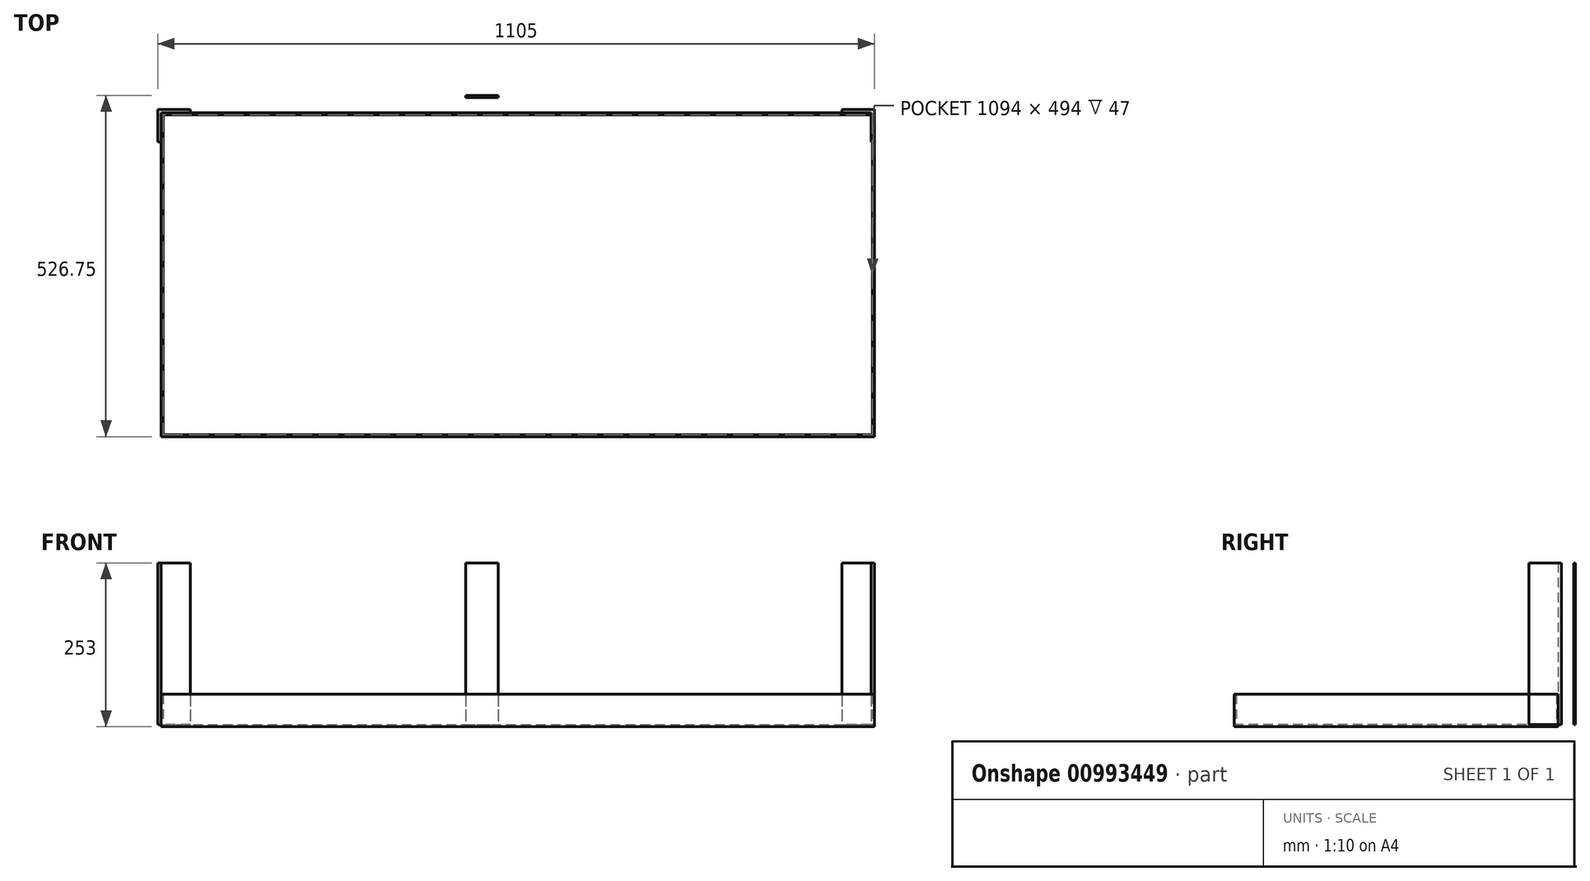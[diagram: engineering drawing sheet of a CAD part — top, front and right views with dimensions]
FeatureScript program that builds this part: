
annotation { "Feature Type Name" : "Feature", "Feature Type Description" : "" }
export const myFeature = defineFeature(function(context is Context, id is Id, definition is map)
    precondition{}
    {
        {
            var Q0;
            Q0=qCreatedBy(makeId("Top.planeOp"),FACE);
            var sketch = newSketch(context, id + "F0", { "sketchPlane" : qUnion([Q0])});
            skLineSegment(sketch, "E0.bottom", {"start": v(-561.99, 291.3) * mm, "end": v(538.01, 291.3) * mm});
            skLineSegment(sketch, "E0.top", {"start": v(-561.99, -208.7) * mm, "end": v(538.01, -208.7) * mm});
            skLineSegment(sketch, "E0.left", {"start": v(-561.99, 291.3) * mm, "end": v(-561.99, -208.7) * mm});
            skLineSegment(sketch, "E0.right", {"start": v(538.01, 291.3) * mm, "end": v(538.01, -208.7) * mm});
            skSolve(sketch);
        }
        {
            var Q0;
            Q0=makeQuery(id+"F0.imprint","IMPRINT",FACE,{"disambiguationData":[TD([[makeQuery(id+"F0.imprint","IMPRINT",EDGE,{"derivedFrom":sQuery(id+"F0.wireOp",EDGE,"E0.bottom")}),-1.0]])]});
            extrude(context, id + "F1", {"entities" : qUnion([Q0]), "depth" : 50 * mm, "offsetDistance" : 25 * mm});
        }
        {
            var Q0;
            Q0=makeQuery(id+"F1.opExtrude","CAP_FACE",FACE,{"disambiguationData":[OSD([sQuery(id+"F0.wireOp",EDGE,"E0.bottom"),sQuery(id+"F0.wireOp",EDGE,"E0.top"),sQuery(id+"F0.wireOp",EDGE,"E0.left"),sQuery(id+"F0.wireOp",EDGE,"E0.right")])],"isStart":false});
            shell(context, id + "F2", {"entities" : qUnion([Q0]), "thickness" : 3 * mm});
        }
        {
            var Q0;
            Q0=makeQuery(id+"F2.opShell","OFFSET_FACE",FACE,{"disambiguationData":[OSD([sQuery(id+"F0.wireOp",EDGE,"E0.bottom"),sQuery(id+"F0.wireOp",EDGE,"E0.top"),sQuery(id+"F0.wireOp",EDGE,"E0.left"),sQuery(id+"F0.wireOp",EDGE,"E0.right")])]});
            var sketch = newSketch(context, id + "F3", { "sketchPlane" : qUnion([Q0])});
            skLineSegment(sketch, "E1", {"start": v(-516.99, 291.3) * mm, "end": v(-516.99, 296.3) * mm});
            skLineSegment(sketch, "E2", {"start": v(-516.99, 296.3) * mm, "end": v(-566.99, 296.3) * mm});
            skLineSegment(sketch, "E3", {"start": v(-566.99, 296.3) * mm, "end": v(-566.99, 246.3) * mm});
            skLineSegment(sketch, "E4", {"start": v(-566.99, 246.3) * mm, "end": v(-561.99, 246.3) * mm});
            skLineSegment(sketch, "E5", {"start": v(-561.99, 246.3) * mm, "end": v(-561.99, 291.3) * mm});
            skLineSegment(sketch, "E6", {"start": v(-561.99, 291.3) * mm, "end": v(-516.99, 291.3) * mm});
            skSolve(sketch);
        }
        {
            var Q0;
            Q0=makeQuery(id+"F3.imprint","IMPRINT",FACE,{"disambiguationData":[TD([[makeQuery(id+"F3.imprint","IMPRINT",EDGE,{"derivedFrom":sQuery(id+"F3.wireOp",EDGE,"E1")}),1.0]])]});
            extrude(context, id + "F4", {"entities" : qUnion([Q0]), "depth" : 250 * mm, "offsetDistance" : 25 * mm});
        }
        {
            var Q0;
            Q0=makeQuery(id+"F4.opExtrude","SWEPT_BODY",BODY,{"disambiguationData":[OSD([sQuery(id+"F3.wireOp",EDGE,"E1"),sQuery(id+"F3.wireOp",EDGE,"E2"),sQuery(id+"F3.wireOp",EDGE,"E3"),sQuery(id+"F3.wireOp",EDGE,"E4"),sQuery(id+"F3.wireOp",EDGE,"E5"),sQuery(id+"F3.wireOp",EDGE,"E6")])]});
            transform(context, id + "F5", {"entities" : qUnion([Q0]), "transformType" : TransformType.TRANSLATION_3D, "dx" : 1105 * mm, "dy" : 0 * mm, "dz" : 0 * mm, "makeCopy" : true});
        }
        {
            var Q0;
            Q0=makeQuery(id+"F5.opPattern","COPY",BODY,{"derivedFrom":makeQuery(id+"F4.opExtrude","SWEPT_BODY",BODY,{"disambiguationData":[OSD([sQuery(id+"F3.wireOp",EDGE,"E1"),sQuery(id+"F3.wireOp",EDGE,"E2"),sQuery(id+"F3.wireOp",EDGE,"E3"),sQuery(id+"F3.wireOp",EDGE,"E4"),sQuery(id+"F3.wireOp",EDGE,"E5"),sQuery(id+"F3.wireOp",EDGE,"E6")])]}),"instanceName":"1"});
            var Q1;
            Q1=makeQuery(id+"F1.opExtrude","SWEPT_FACE",FACE,{"disambiguationData":[OSD([sQuery(id+"F0.wireOp",EDGE,"E0.right")])]});
            mirror(context, id + "F6", {"entities" : qUnion([Q0]), "mirrorPlane" : qUnion([Q1])});
        }
        {
            var Q0;
            Q0=makeQuery(id+"F5.opPattern","COPY",BODY,{"derivedFrom":makeQuery(id+"F4.opExtrude","SWEPT_BODY",BODY,{"disambiguationData":[OSD([sQuery(id+"F3.wireOp",EDGE,"E1"),sQuery(id+"F3.wireOp",EDGE,"E2"),sQuery(id+"F3.wireOp",EDGE,"E3"),sQuery(id+"F3.wireOp",EDGE,"E4"),sQuery(id+"F3.wireOp",EDGE,"E5"),sQuery(id+"F3.wireOp",EDGE,"E6")])]}),"instanceName":"1"});
            deleteBodies(context, id + "F7", {"entities" : qUnion([Q0])});
        }
        {
            var Q0;
            Q0=makeQuery(id+"F2.opShell","OFFSET_FACE",FACE,{"disambiguationData":[OSD([sQuery(id+"F0.wireOp",EDGE,"E0.bottom"),sQuery(id+"F0.wireOp",EDGE,"E0.top"),sQuery(id+"F0.wireOp",EDGE,"E0.left"),sQuery(id+"F0.wireOp",EDGE,"E0.right")])]});
            var sketch = newSketch(context, id + "F8", { "sketchPlane" : qUnion([Q0])});
            skLineSegment(sketch, "E7.bottom", {"start": v(-92.4, 318.05) * mm, "end": v(-42.4, 318.05) * mm});
            skLineSegment(sketch, "E7.top", {"start": v(-92.4, 315.05) * mm, "end": v(-42.4, 315.05) * mm});
            skLineSegment(sketch, "E7.left", {"start": v(-92.4, 318.05) * mm, "end": v(-92.4, 315.05) * mm});
            skLineSegment(sketch, "E7.right", {"start": v(-42.4, 318.05) * mm, "end": v(-42.4, 315.05) * mm});
            skSolve(sketch);
        }
        {
            var Q0;
            Q0=makeQuery(id+"F8.imprint","IMPRINT",FACE,{"disambiguationData":[TD([[makeQuery(id+"F8.imprint","IMPRINT",EDGE,{"derivedFrom":sQuery(id+"F8.wireOp",EDGE,"E7.bottom")}),-1.0]])]});
            extrude(context, id + "F9", {"entities" : qUnion([Q0]), "depth" : 250 * mm, "offsetDistance" : 25 * mm});
        }
    });
